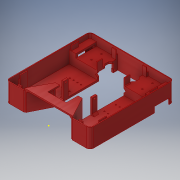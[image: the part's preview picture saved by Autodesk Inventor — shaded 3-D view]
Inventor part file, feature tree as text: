
AUTODESK INVENTOR PART (.ipt)
format: ipt  version: 2019 (Build 230136000, 136)  size: 772,096 bytes
history: native  units: in
note: dims shown in document units (in); Inventor stores cm internally (conversion verified against a paired STEP export)
features: extrude x38, sketch x38, mirror x9, chamfer x6, fillet x4, plane x3
ambient origin geometry x8: Origin, YZ Plane, XZ Plane, XY Plane, X Axis, Y Axis, Z Axis, Center Point
bodies: Solid1 (feature_tree)
feature tree (98):
  extrude  "Extrusion1"  Depth=1.422in
  extrude  "Extrusion2"  Depth=2.953in
  extrude  "Extrusion3"  Depth=0.1969in TaperAngle=0.0deg
  extrude  "Extrusion4"  Depth=0.1969in
  extrude  "Extrusion5"  Depth=2.25in
  extrude  "Extrusion6"  Depth=0.4134in TaperAngle=0.0deg
  extrude  "Extrusion7"  Depth=0.1969in
  extrude  "Extrusion8"  Depth=0.1969in
  extrude  "Extrusion9"  Depth=0.4134in
  extrude  "Extrusion10"  Depth=0.9843in
  extrude  "Extrusion11"  Depth=0.1575in
  extrude  "Extrusion12"  Depth=1.0in TaperAngle=0.0deg
  extrude  "Extrusion13"  Depth=0.1969in
  mirror  "Mirror1"
  extrude  "Extrusion14"  Depth=0.886in
  extrude  "Extrusion15"  Depth=0.7874in
  mirror  "Mirror2"
  sketch  "Sketch18"  dims[d39=1.6142in d40=1.5748in]
  extrude  "Extrusion16"  Depth=1.5748in
  extrude  "Extrusion17"  Depth=0.6102in
  extrude  "Extrusion18"  Depth=0.2362in
  plane  "Work Plane1"
  extrude  "Extrusion19"  Depth=0.6102in
  plane  "Work Plane2"
  extrude  "Extrusion20"  Depth=0.886in TaperAngle=0.0deg
  extrude  "Extrusion21"  Depth=0.4528in
  fillet  "Fillet8"  Radius=0.9055in
  extrude  "Extrusion22"  TaperAngle=135.0deg  [1 undecoded]
  extrude  "Extrusion26"  Depth=0.1181in
  extrude  "Extrusion24"  Depth=0.1969in TaperAngle=0.0deg
  extrude  "Extrusion27"  Depth=5.25in
  fillet  "Fillet9"  Radius=0.1969in
  extrude  "Extrusion28"  Depth=1.65in TaperAngle=0.0deg
  chamfer  "Chamfer1"  Distance=0.3937in
  chamfer  "Chamfer2"  Distance=0.2362in
  extrude  "Extrusion29"  Depth=0.1575in
  extrude  "Extrusion25"  Depth=0.2362in TaperAngle=0.0deg
  extrude  "Extrusion30"  Depth=1.9685in
  sketch  "Sketch36"  dims[d74=0.1575in d75=0.3937in d76=0.0in]
  plane  "Work Plane3"
  mirror  "Mirror4"
  fillet  "Fillet10"  [1 undecoded]
  mirror  "Mirror5"
  fillet  "Fillet11"  Radius=1.9685in
  chamfer  "Chamfer3"  Distance=0.3937in
  extrude  "Extrusion31"  TaperAngle=90.0deg  [1 undecoded]
  extrude  "Extrusion32"  TaperAngle=180.0deg  [1 undecoded]
  mirror  "Mirror6"
  extrude  "Extrusion33"  TaperAngle=90.0deg  [1 undecoded]
  extrude  "Extrusion34"  Depth=0.1575in
  mirror  "Mirror7"
  extrude  "Extrusion35"  Depth=1.9685in TaperAngle=0.0deg
  mirror  "Mirror8"
  extrude  "Extrusion36"  Depth=7.874in
  chamfer  "Chamfer4"  Angle=90.0deg  [1 undecoded]
  extrude  "Extrusion37"  Depth=0.9843in
  chamfer  "Chamfer5"  Distance=1.9685in
  mirror  "Mirror9"
  extrude  "Extrusion38"  Depth=1.9685in TaperAngle=0.0deg
  mirror  "Mirror10"
  chamfer  "Chamfer6"  Distance=0.0787in
  extrude  "Extrusion39"  Depth=0.6in
  sketch  "Sketch1"  dims[d0=1.422in d1=2.17in]
  sketch  "Sketch3"  dims[d2=1.422in d3=2.953in]
  sketch  "Sketch4"  dims[d4=6.75in d5=0.1969in d6=0.0in]
  sketch  "Sketch5"  dims[d7=2.953in d8=0.1969in]
  sketch  "Sketch6"  dims[d9=1.2992in d10=0.0in d11=2.25in]
  sketch  "Sketch8"  dims[d12=0.1969in d13=0.4134in d14=0.0in]
  sketch  "Sketch9"  dims[d15=0.1969in d16=0.1969in]
  sketch  "Sketch10"  dims[d17=2.0in d18=0.0in d19=0.1969in]
  sketch  "Sketch11"  dims[d20=0.4134in d21=0.0in d22=1.68in]
  sketch  "Sketch12"  dims[d23=0.9843in d24=0.5315in]
  sketch  "Sketch13"  dims[d25=1.063in d26=0.1575in]
  sketch  "Sketch14"  dims[d27=0.1575in d28=1.0in d29=0.0in]
  sketch  "Sketch15"  dims[d32=2.25in d33=0.1969in]
  sketch  "Sketch16"  dims[d34=0.886in d35=0.0in d36=2.7638in]
  sketch  "Sketch17"  dims[d37=4.0787in d38=0.7874in]
  sketch  "Sketch19"  dims[d41=0.2362in d42=0.6102in]
  sketch  "Sketch20"  dims[d43=0.1378in d44=0.2362in]
  sketch  "Sketch22"  dims[d45=0.6102in d46=0.1378in]
  sketch  "Sketch25"  dims[d47=1.5748in d49=0.3937in d50=0.3937in d52=1.0in d54=0.886in d55=0.0in]
  sketch  "Sketch26"  dims[d56=0.4528in d57=0.4528in d58=0.9055in]
  sketch  "Sketch28"  dims[d59=0.2953in d60=135.0deg]
  sketch  "Sketch29"  dims[d61=0.5906in d62=0.1181in]
  sketch  "Sketch30"  dims[d63=0.1181in d64=0.1969in d65=0.0in]
  sketch  "Sketch31"  dims[d66=0.1969in d67=5.25in d68=0.1969in]
  sketch  "Sketch33"  dims[d69=0.5in d70=1.65in d71=0.0in]
  sketch  "Sketch34"  dims[d72=0.25in]
  sketch  "Sketch35"  dims[d73=0.1969in]
  sketch  "Sketch39"  dims[d77=0.1969in d78=0.2362in d79=0.0in]
  sketch  "Sketch41"  dims[d80=0.1181in d81=0.1575in]
  sketch  "Sketch42"  dims[d82=0.1575in d83=0.2362in d84=0.0in]
  sketch  "Sketch43"  dims[d94=1.9685in d96=1.9685in d97=0.0in d98=1.9685in d99=0.3937in d100=0.0in]
  sketch  "Sketch44"  dims[d102=7.874in d103=90.0deg]
  sketch  "Sketch45"  dims[d104=0.1575in d105=180.0deg]
  sketch  "Sketch46"  dims[d106=0.1575in d107=90.0deg]
  sketch  "Sketch47"  dims[d108=1.9685in d109=0.0in d110=0.1575in]
  sketch  "Sketch48"  dims[d111=1.9685in d112=0.0in d113=1.9685in d114=0.0in d115=7.874in d116=90.0deg d117=0.9843in d118=1.9685in d119=1.9685in d120=0.0in d124=0.0787in d125=0.0in d126=0.6in d127=0.0787in d128=0.0in d133=2.0in d140=0.0787in d141=0.0in d142=2.0in d143=0.3937in d144=0.0787in d145=0.0787in d146=180.0deg d147=0.3937in d148=0.0787in d149=0.0in d154=1.0in d155=0.6in d156=0.1969in d157=0.0in d158=1.0in d159=0.6in d160=0.1969in d161=0.0in d163=0.0787in d164=0.0in d165=0.0787in d166=0.0in d167=2.0in d168=0.3937in d169=0.0787in d170=0.0787in d171=0.3937in d172=0.0787in d173=0.0in d174=0.0787in d175=0.0787in d176=45.0deg d177=0.1969in d178=0.0787in d179=45.0deg d180=2.0in d181=0.0787in d182=0.0in d183=2.0in d184=0.0787in d185=0.0in d186=0.3937in d187=0.1181in d188=0.1969in d189=0.0787in d190=45.0deg d191=0.3937in d192=0.15in d193=0.3937in d194=0.15in d195=0.0787in d196=0.0in d197=0.9843in d198=0.15in d199=0.7874in d200=0.7874in d201=0.3937in d202=0.15in d203=0.0787in d204=0.0in d205=0.3937in d206=0.0787in d207=0.3937in d208=0.0787in d209=0.0787in d210=0.0in d211=0.0787in d212=0.0787in d213=0.7874in d214=0.0787in d215=0.0in d216=0.15in d217=180.0deg d218=0.0787in d219=0.7874in d220=0.0787in d221=0.0in d222=0.5315in d223=0.7874in d224=90.0deg d225=0.3937in d226=0.1969in d227=0.0in d228=0.1969in d229=0.0787in d230=45.0deg d231=0.4429in d232=90.0deg d233=0.3937in d234=90.0deg d235=0.3937in d236=0.1969in d237=0.0in d238=0.1969in d239=0.0787in d240=45.0deg d241=0.0787in d242=0.5906in d243=0.3937in d244=0.0in d245=0.0787in d246=0.0787in d247=45.0deg d248=0.1969in d249=0.315in d250=0.1969in d251=0.315in d252=0.0591in d253=0.0in]
note: 6 required parameter values undecoded (feature->parameter linkage not recoverable at this tier; creation-order binding heuristic only, values carry confidence <= 0.55)
